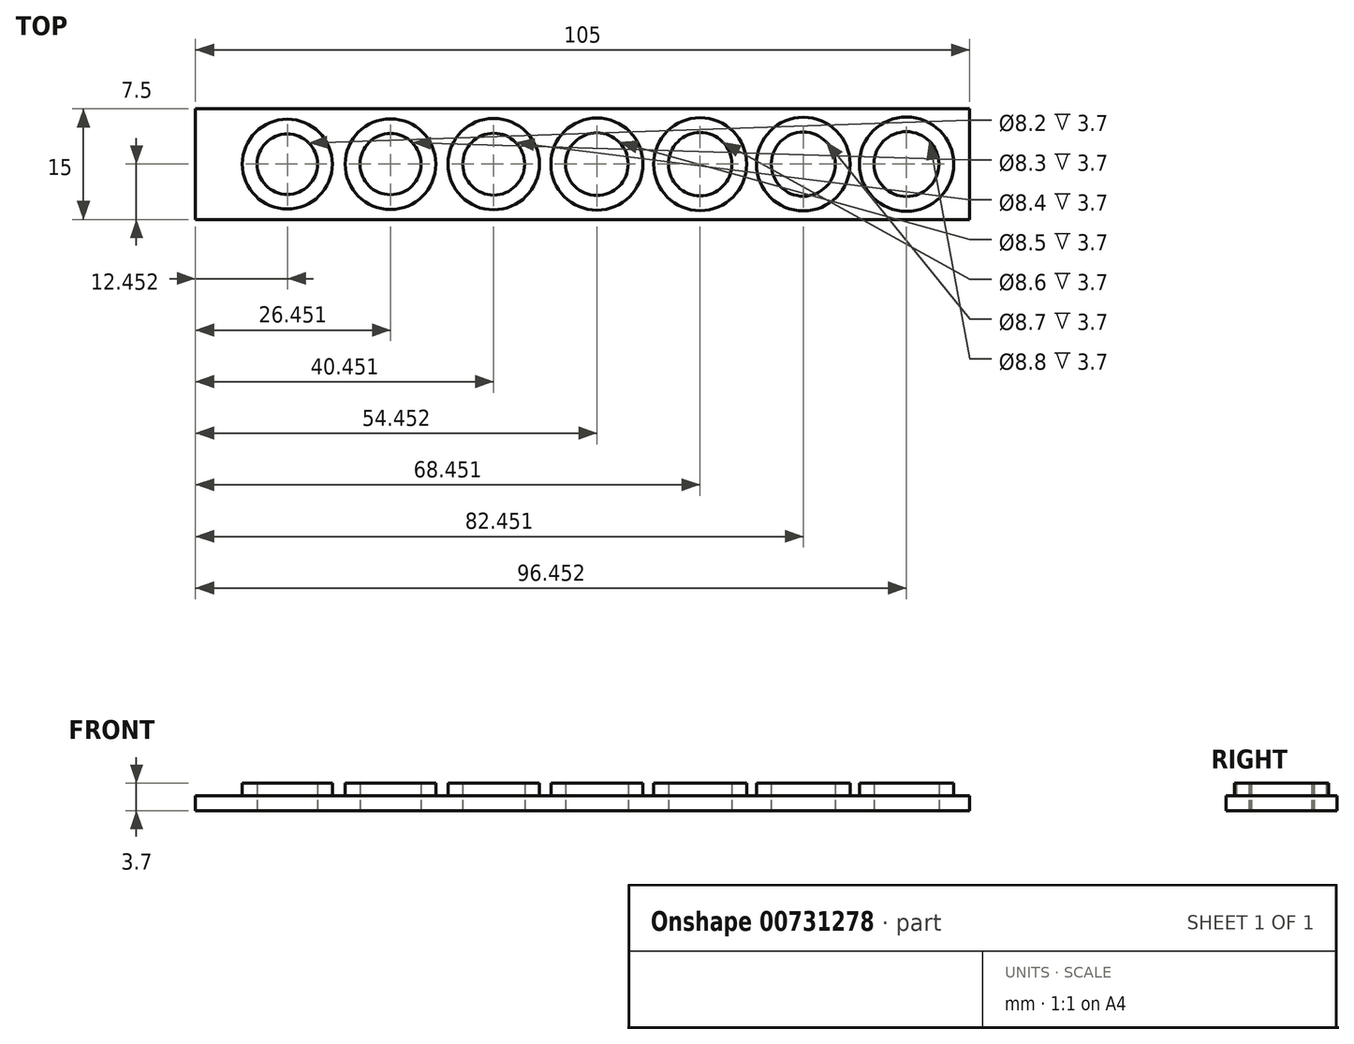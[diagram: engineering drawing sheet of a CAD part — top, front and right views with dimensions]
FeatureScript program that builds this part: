
annotation { "Feature Type Name" : "Feature", "Feature Type Description" : "" }
export const myFeature = defineFeature(function(context is Context, id is Id, definition is map)
    precondition{}
    {
        {
            var Q0;
            Q0=qCreatedBy(makeId("Top.planeOp"),FACE);
            var sketch = newSketch(context, id + "F0", { "sketchPlane" : qUnion([Q0])});
            skLineSegment(sketch, "E0.bottom", {"start": v(-52.5, 7.5) * mm, "end": v(52.5, 7.5) * mm});
            skLineSegment(sketch, "E0.top", {"start": v(-52.5, -7.5) * mm, "end": v(52.5, -7.5) * mm});
            skLineSegment(sketch, "E0.left", {"start": v(-52.5, 7.5) * mm, "end": v(-52.5, -7.5) * mm});
            skLineSegment(sketch, "E0.right", {"start": v(52.5, 7.5) * mm, "end": v(52.5, -7.5) * mm});
            skPoint(sketch, "E0.middle", {"position": v(0, 0) * mm});
            skCircle(sketch, "E1", {"center": v(-40.05, 0) * mm, "radius": 4.1 * mm});
            skCircle(sketch, "E2", {"center": v(-26.05, 0) * mm, "radius": 4.15 * mm});
            skCircle(sketch, "E3", {"center": v(-12.05, 0) * mm, "radius": 4.2 * mm});
            skCircle(sketch, "E4", {"center": v(1.95, 0) * mm, "radius": 4.25 * mm});
            skCircle(sketch, "E5", {"center": v(15.95, 0) * mm, "radius": 4.3 * mm});
            skCircle(sketch, "E6", {"center": v(29.95, 0) * mm, "radius": 4.35 * mm});
            skCircle(sketch, "E7", {"center": v(43.95, 0) * mm, "radius": 4.4 * mm});
            skCircle(sketch, "E8.0", {"center": v(-40.05, 0) * mm, "radius": 6.1 * mm});
            skCircle(sketch, "E9.0", {"center": v(-26.05, 0) * mm, "radius": 6.15 * mm});
            skCircle(sketch, "E10.0", {"center": v(-12.05, 0) * mm, "radius": 6.2 * mm});
            skCircle(sketch, "E11.0", {"center": v(1.95, 0) * mm, "radius": 6.25 * mm});
            skCircle(sketch, "E12.0", {"center": v(15.95, 0) * mm, "radius": 6.3 * mm});
            skCircle(sketch, "E13.0", {"center": v(29.95, 0) * mm, "radius": 6.35 * mm});
            skCircle(sketch, "E14.0", {"center": v(43.95, 0) * mm, "radius": 6.4 * mm});
            skSolve(sketch);
        }
        {
            var Q0;
            Q0=makeQuery(id+"F0.imprint","IMPRINT",FACE,{"disambiguationData":[TD([[makeQuery(id+"F0.imprint","IMPRINT",EDGE,{"derivedFrom":sQuery(id+"F0.wireOp",EDGE,"E0.bottom")}),-1.0]])]});
            extrude(context, id + "F1", {"entities" : qUnion([Q0]), "depth" : 2 * mm, "offsetDistance" : 25 * mm});
        }
        {
            var Q0;
            Q0=makeQuery(id+"F0.imprint","IMPRINT",FACE,{"disambiguationData":[TD([[makeQuery(id+"F0.imprint","IMPRINT",EDGE,{"derivedFrom":sQuery(id+"F0.wireOp",EDGE,"E1")}),-1.0]])]});
            var Q1;
            Q1=makeQuery(id+"F0.imprint","IMPRINT",FACE,{"disambiguationData":[TD([[makeQuery(id+"F0.imprint","IMPRINT",EDGE,{"derivedFrom":sQuery(id+"F0.wireOp",EDGE,"E2")}),-1.0]])]});
            var Q2;
            Q2=makeQuery(id+"F0.imprint","IMPRINT",FACE,{"disambiguationData":[TD([[makeQuery(id+"F0.imprint","IMPRINT",EDGE,{"derivedFrom":sQuery(id+"F0.wireOp",EDGE,"E3")}),-1.0]])]});
            var Q3;
            Q3=makeQuery(id+"F0.imprint","IMPRINT",FACE,{"disambiguationData":[TD([[makeQuery(id+"F0.imprint","IMPRINT",EDGE,{"derivedFrom":sQuery(id+"F0.wireOp",EDGE,"E4")}),-1.0]])]});
            var Q4;
            Q4=makeQuery(id+"F0.imprint","IMPRINT",FACE,{"disambiguationData":[TD([[makeQuery(id+"F0.imprint","IMPRINT",EDGE,{"derivedFrom":sQuery(id+"F0.wireOp",EDGE,"E5")}),-1.0]])]});
            var Q5;
            Q5=makeQuery(id+"F0.imprint","IMPRINT",FACE,{"disambiguationData":[TD([[makeQuery(id+"F0.imprint","IMPRINT",EDGE,{"derivedFrom":sQuery(id+"F0.wireOp",EDGE,"E6")}),-1.0]])]});
            var Q6;
            Q6=makeQuery(id+"F0.imprint","IMPRINT",FACE,{"disambiguationData":[TD([[makeQuery(id+"F0.imprint","IMPRINT",EDGE,{"derivedFrom":sQuery(id+"F0.wireOp",EDGE,"E7")}),-1.0]])]});
            extrude(context, id + "F2", {"entities" : qUnion([Q0, Q1, Q2, Q3, Q4, Q5, Q6]), "operationType" : NewBodyOperationType.ADD, "depth" : 3.7 * mm, "offsetDistance" : 25 * mm});
        }
    });
